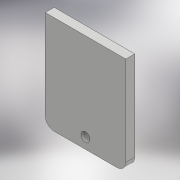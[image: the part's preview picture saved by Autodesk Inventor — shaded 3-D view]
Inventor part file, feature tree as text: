
AUTODESK INVENTOR PART (.ipt)
format: ipt  version: 2017 (Build 210142000, 142)  size: 175,104 bytes
history: native  units: mm
features: extrude x5, sketch x5, projected_geometry x2, fillet x1
ambient origin geometry x8: Origin, YZ Plane, XZ Plane, XY Plane, X Axis, Y Axis, Z Axis, Center Point
bodies: Solid1 (feature_tree)
feature tree (13):
  extrude  "Extrusion1"  Depth=2.0mm TaperAngle=0.0deg
  extrude  "Extrusion5"  Depth=0.5mm TaperAngle=0.0deg
  extrude  "Extrusion6"  Depth=2.0mm
  extrude  "Extrusion7"  Depth=2.0mm
  extrude  "Extrusion8"  [1 undecoded]
  fillet  "Fillet1"  [1 undecoded]
  sketch  "Sketch1"  dims[d0=18.0mm d1=22.0mm d2=3.0mm d3=0.5mm d4=16.0mm d5=2.0mm d6=0.0mm d16=2.0mm d17=0.0mm]
  sketch  "Sketch8"  dims[d19=4.0mm d20=0.5mm d21=0.0mm]
  projected_geometry  "Projected Loop3"
  sketch  "Sketch9"  dims[d26=2.0mm d27=0.0mm d28=2.0mm]
  projected_geometry  "Projected Loop4"
  sketch  "Sketch11"  dims[d29=2.0mm d30=0.0mm d31=2.0mm]
  sketch  "Sketch12"
note: 2 required parameter values undecoded (feature->parameter linkage not recoverable at this tier; creation-order binding heuristic only, values carry confidence <= 0.55)
